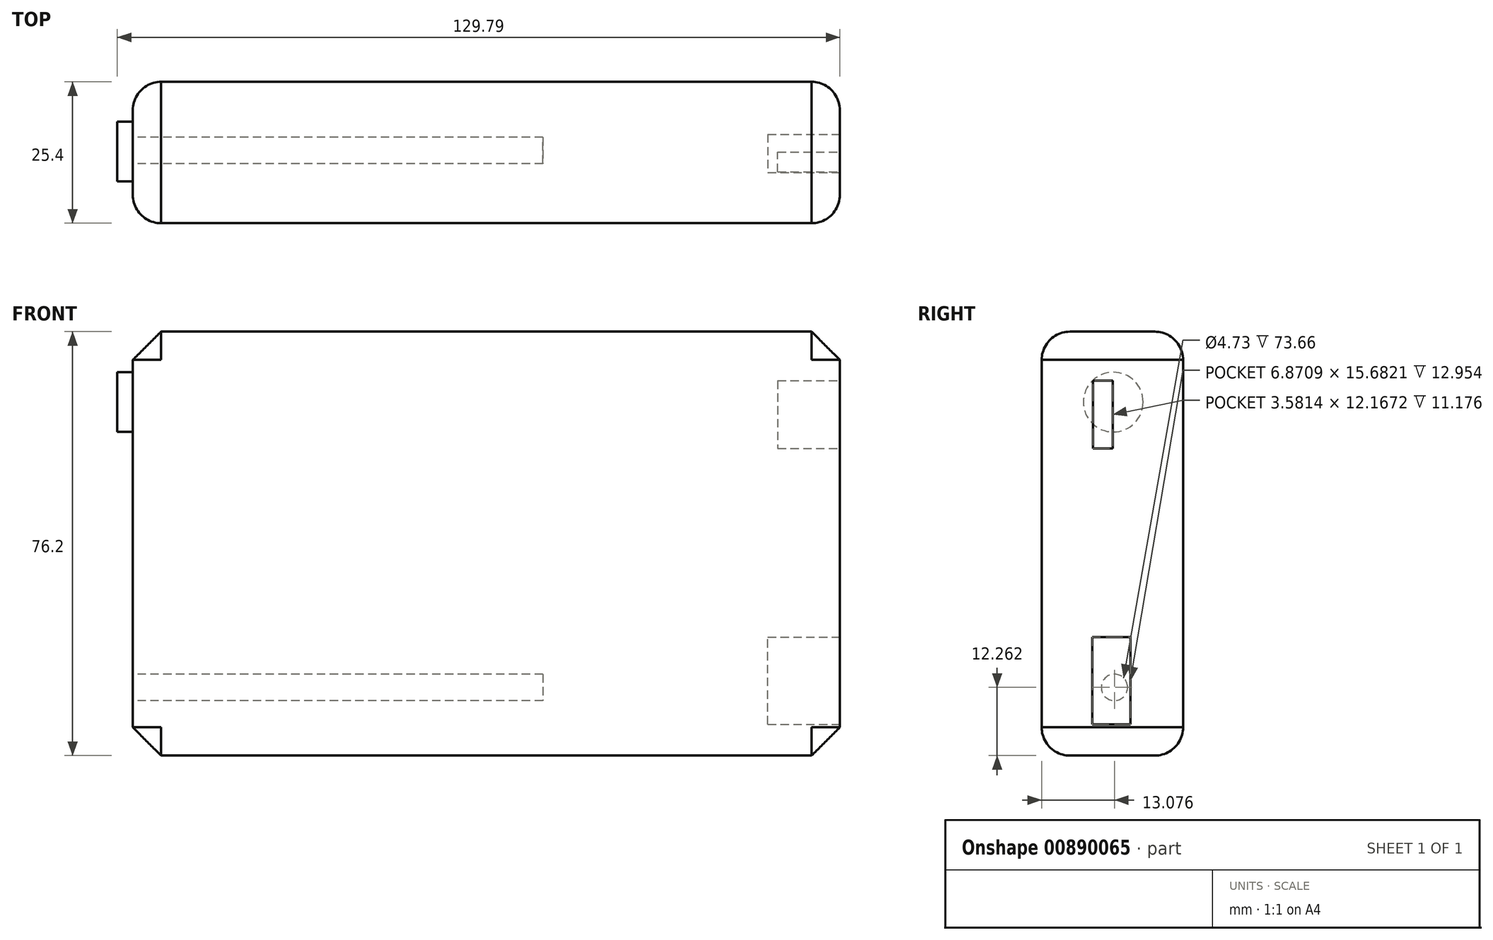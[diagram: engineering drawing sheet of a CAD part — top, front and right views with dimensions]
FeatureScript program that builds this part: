
annotation { "Feature Type Name" : "Feature", "Feature Type Description" : "" }
export const myFeature = defineFeature(function(context is Context, id is Id, definition is map)
    precondition{}
    {
        {
            var Q0;
            Q0=qCreatedBy(makeId("Front.planeOp"),FACE);
            var sketch = newSketch(context, id + "F0", { "sketchPlane" : qUnion([Q0])});
            skLineSegment(sketch, "E0.bottom", {"start": v(-63.5, 38.1) * mm, "end": v(63.5, 38.1) * mm});
            skLineSegment(sketch, "E0.top", {"start": v(-63.5, -38.1) * mm, "end": v(63.5, -38.1) * mm});
            skLineSegment(sketch, "E0.left", {"start": v(-63.5, 38.1) * mm, "end": v(-63.5, -38.1) * mm});
            skLineSegment(sketch, "E0.right", {"start": v(63.5, 38.1) * mm, "end": v(63.5, -38.1) * mm});
            skPoint(sketch, "E0.middle", {"position": v(0, 0) * mm});
            skSolve(sketch);
        }
        {
            var Q0;
            Q0=makeQuery(id+"F0.imprint","IMPRINT",FACE,{"disambiguationData":[TD([[makeQuery(id+"F0.imprint","IMPRINT",EDGE,{"derivedFrom":sQuery(id+"F0.wireOp",EDGE,"E0.bottom")}),-1.0]])]});
            extrude(context, id + "F1", {"entities" : qUnion([Q0]), "depth" : 25.4 * mm, "offsetDistance" : 25.4 * mm});
        }
        {
            var Q0;
            Q0=makeQuery(id+"F1.opExtrude","CAP_FACE",FACE,{"disambiguationData":[OSD([sQuery(id+"F0.wireOp",EDGE,"E0.bottom"),sQuery(id+"F0.wireOp",EDGE,"E0.top"),sQuery(id+"F0.wireOp",EDGE,"E0.left"),sQuery(id+"F0.wireOp",EDGE,"E0.right")])],"isStart":false});
            fillet(context, id + "F2", {"entities" : qUnion([Q0]), "radius" : 5.08 * mm, "tangentPropagation" : true, "allowEdgeOverflow" : false});
        }
        {
            var Q0;
            Q0=makeQuery(id+"F1.opExtrude","CAP_FACE",FACE,{"disambiguationData":[OSD([sQuery(id+"F0.wireOp",EDGE,"E0.bottom"),sQuery(id+"F0.wireOp",EDGE,"E0.top"),sQuery(id+"F0.wireOp",EDGE,"E0.left"),sQuery(id+"F0.wireOp",EDGE,"E0.right")])],"isStart":true});
            fillet(context, id + "F3", {"entities" : qUnion([Q0]), "radius" : 5.08 * mm, "tangentPropagation" : true, "allowEdgeOverflow" : false});
        }
        {
            var Q0;
            Q0=makeQuery(id+"F1.opExtrude","SWEPT_FACE",FACE,{"disambiguationData":[OSD([sQuery(id+"F0.wireOp",EDGE,"E0.right")])]});
            var sketch = newSketch(context, id + "F4", { "sketchPlane" : qUnion([Q0])});
            skLineSegment(sketch, "E1.bottom", {"start": v(-9.42, -32.5) * mm, "end": v(-16.29, -32.5) * mm});
            skLineSegment(sketch, "E1.top", {"start": v(-9.42, -16.81) * mm, "end": v(-16.29, -16.81) * mm});
            skLineSegment(sketch, "E1.left", {"start": v(-9.42, -32.5) * mm, "end": v(-9.42, -16.81) * mm});
            skLineSegment(sketch, "E1.right", {"start": v(-16.29, -32.5) * mm, "end": v(-16.29, -16.81) * mm});
            skSolve(sketch);
        }
        {
            var Q0;
            Q0=makeQuery(id+"F4.imprint","IMPRINT",FACE,{"disambiguationData":[TD([[makeQuery(id+"F4.imprint","IMPRINT",EDGE,{"derivedFrom":sQuery(id+"F4.wireOp",EDGE,"E1.bottom")}),-1.0]])]});
            extrude(context, id + "F5", {"entities" : qUnion([Q0]), "operationType" : NewBodyOperationType.REMOVE, "oppositeDirection" : true, "depth" : 12.95 * mm, "offsetDistance" : 25.4 * mm});
        }
        {
            var Q0;
            Q0=makeQuery(id+"F1.opExtrude","SWEPT_FACE",FACE,{"disambiguationData":[OSD([sQuery(id+"F0.wireOp",EDGE,"E0.right")])]});
            var sketch = newSketch(context, id + "F6", { "sketchPlane" : qUnion([Q0])});
            skLineSegment(sketch, "E2.bottom", {"start": v(-16.2, 29.3) * mm, "end": v(-12.62, 29.3) * mm});
            skLineSegment(sketch, "E2.top", {"start": v(-16.2, 17.13) * mm, "end": v(-12.62, 17.13) * mm});
            skLineSegment(sketch, "E2.left", {"start": v(-16.2, 29.3) * mm, "end": v(-16.2, 17.13) * mm});
            skLineSegment(sketch, "E2.right", {"start": v(-12.62, 29.3) * mm, "end": v(-12.62, 17.13) * mm});
            skSolve(sketch);
        }
        {
            var Q0;
            Q0=makeQuery(id+"F6.imprint","IMPRINT",FACE,{"disambiguationData":[TD([[makeQuery(id+"F6.imprint","IMPRINT",EDGE,{"derivedFrom":sQuery(id+"F6.wireOp",EDGE,"E2.bottom")}),-1.0]])]});
            extrude(context, id + "F7", {"entities" : qUnion([Q0]), "operationType" : NewBodyOperationType.REMOVE, "oppositeDirection" : true, "depth" : 11.18 * mm, "offsetDistance" : 25.4 * mm});
        }
        {
            var Q0;
            Q0=makeQuery(id+"F1.opExtrude","SWEPT_EDGE",EDGE,{"disambiguationData":[OSD([sQuery(id+"F0.wireOp",EDGE,"E0.bottom"),sQuery(id+"F0.wireOp",EDGE,"E0.left")])]});
            chamfer(context, id + "F8", {"entities" : qUnion([Q0]), "width" : 5.08 * mm, "tangentPropagation" : true});
        }
        {
            var Q0;
            Q0=makeQuery(id+"F1.opExtrude","SWEPT_EDGE",EDGE,{"disambiguationData":[OSD([sQuery(id+"F0.wireOp",EDGE,"E0.bottom"),sQuery(id+"F0.wireOp",EDGE,"E0.right")])]});
            chamfer(context, id + "F9", {"entities" : qUnion([Q0]), "width" : 5.08 * mm, "tangentPropagation" : true});
        }
        {
            var Q0;
            Q0=makeQuery(id+"F1.opExtrude","SWEPT_EDGE",EDGE,{"disambiguationData":[OSD([sQuery(id+"F0.wireOp",EDGE,"E0.top"),sQuery(id+"F0.wireOp",EDGE,"E0.right")])]});
            chamfer(context, id + "F10", {"entities" : qUnion([Q0]), "width" : 5.08 * mm, "tangentPropagation" : true});
        }
        {
            var Q0;
            Q0=makeQuery(id+"F1.opExtrude","SWEPT_EDGE",EDGE,{"disambiguationData":[OSD([sQuery(id+"F0.wireOp",EDGE,"E0.top"),sQuery(id+"F0.wireOp",EDGE,"E0.left")])]});
            chamfer(context, id + "F11", {"entities" : qUnion([Q0]), "width" : 5.08 * mm, "tangentPropagation" : true});
        }
        {
            var Q0;
            Q0=makeQuery(id+"F1.opExtrude","SWEPT_FACE",FACE,{"disambiguationData":[OSD([sQuery(id+"F0.wireOp",EDGE,"E0.left")])]});
            var sketch = newSketch(context, id + "F12", { "sketchPlane" : qUnion([Q0])});
            skCircle(sketch, "E3", {"center": v(12.54, 25.44) * mm, "radius": 5.37 * mm});
            skCircle(sketch, "E4", {"center": v(12.75, 16.03) * mm, "radius": 1.99 * mm});
            skSolve(sketch);
        }
        {
            var Q0;
            Q0=makeQuery(id+"F12.imprint","IMPRINT",FACE,{"disambiguationData":[TD([[makeQuery(id+"F12.imprint","IMPRINT",EDGE,{"derivedFrom":sQuery(id+"F12.wireOp",EDGE,"E3")}),1.0]])]});
            extrude(context, id + "F13", {"entities" : qUnion([Q0]), "depth" : 2.8 * mm, "offsetDistance" : 25.4 * mm});
        }
        {
            var Q0;
            Q0=makeQuery(id+"F1.opExtrude","SWEPT_FACE",FACE,{"disambiguationData":[OSD([sQuery(id+"F0.wireOp",EDGE,"E0.left")])]});
            var sketch = newSketch(context, id + "F14", { "sketchPlane" : qUnion([Q0])});
            skCircle(sketch, "E5", {"center": v(12.32, -25.84) * mm, "radius": 2.37 * mm});
            skSolve(sketch);
        }
        {
            var Q0;
            Q0=makeQuery(id+"F14.imprint","IMPRINT",FACE,{"disambiguationData":[TD([[makeQuery(id+"F14.imprint","IMPRINT",EDGE,{"derivedFrom":sQuery(id+"F14.wireOp",EDGE,"E5")}),1.0]])]});
            extrude(context, id + "F15", {"entities" : qUnion([Q0]), "operationType" : NewBodyOperationType.REMOVE, "oppositeDirection" : true, "depth" : 73.66 * mm, "offsetDistance" : 25.4 * mm});
        }
    });
